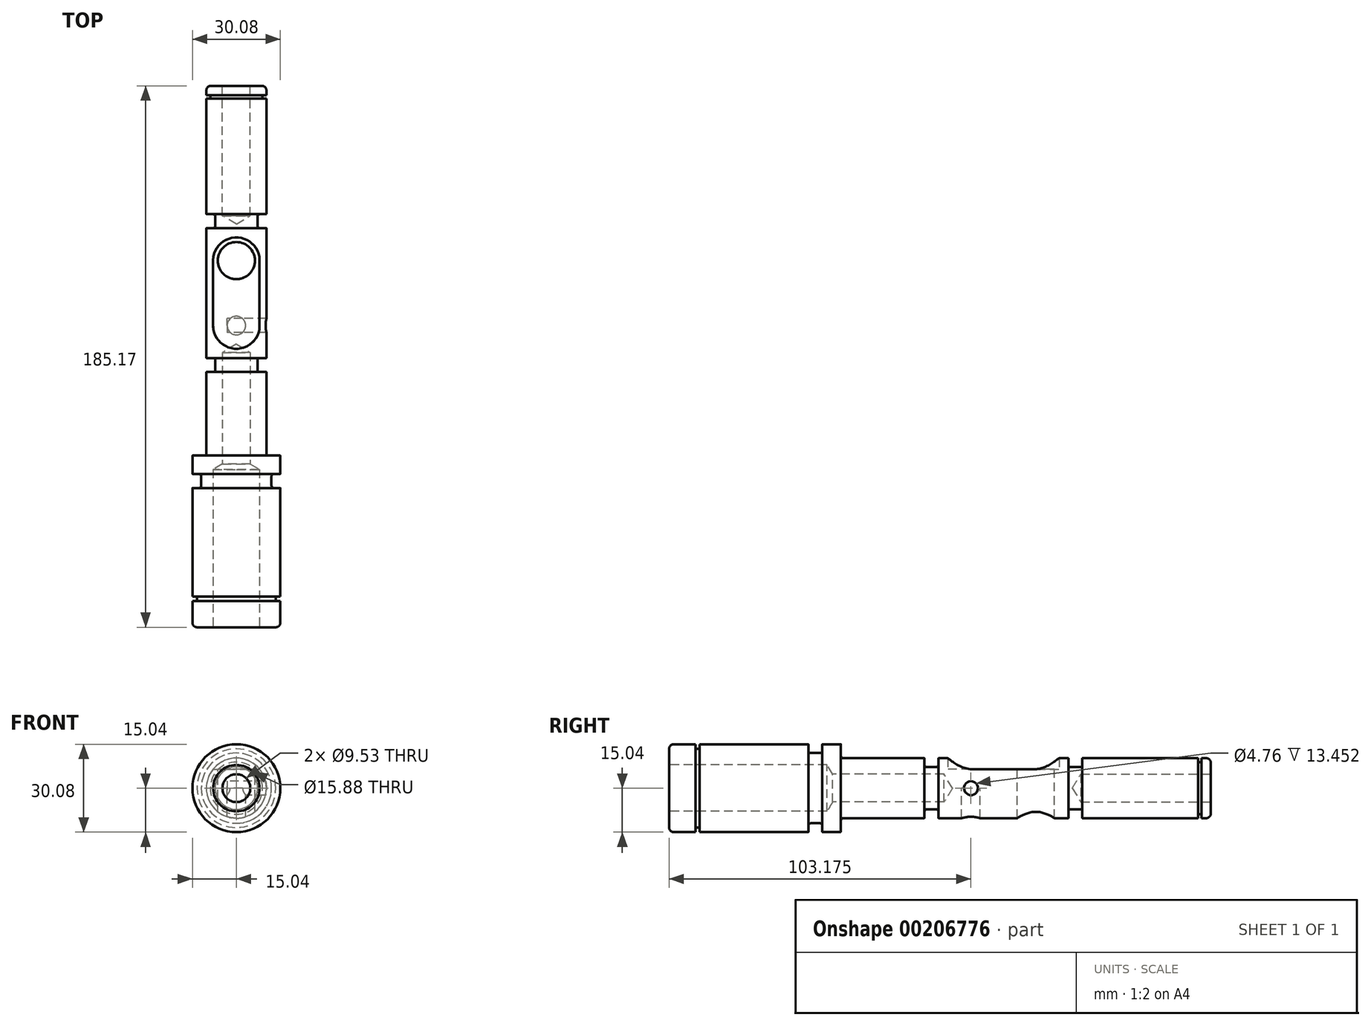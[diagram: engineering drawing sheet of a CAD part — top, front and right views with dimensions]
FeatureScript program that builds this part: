
annotation { "Feature Type Name" : "Feature", "Feature Type Description" : "" }
export const myFeature = defineFeature(function(context is Context, id is Id, definition is map)
    precondition{}
    {
        {
            var Q0;
            Q0=qCreatedBy(makeId("Right.planeOp"),FACE);
            var sketch = newSketch(context, id + "F0", { "sketchPlane" : qUnion([Q0])});
            skLineSegment(sketch, "E0", {"start": v(0, 0) * mm, "end": v(0, 15.04) * mm});
            skLineSegment(sketch, "E1", {"start": v(0, 15.04) * mm, "end": v(9.02, 15.04) * mm});
            skLineSegment(sketch, "E2", {"start": v(47.63, 12) * mm, "end": v(47.63, 15.04) * mm});
            skLineSegment(sketch, "E3", {"start": v(47.63, 12) * mm, "end": v(52.37, 12) * mm});
            skLineSegment(sketch, "E4", {"start": v(52.37, 15.04) * mm, "end": v(52.37, 12) * mm});
            skLineSegment(sketch, "E5", {"start": v(52.37, 15.04) * mm, "end": v(58.72, 15.04) * mm});
            skLineSegment(sketch, "E6", {"start": v(87.3, 10.27) * mm, "end": v(87.3, 7.24) * mm});
            skLineSegment(sketch, "E7", {"start": v(87.3, 7.24) * mm, "end": v(92.05, 7.24) * mm});
            skLineSegment(sketch, "E8", {"start": v(92.05, 7.24) * mm, "end": v(92.05, 10.27) * mm});
            skLineSegment(sketch, "E9", {"start": v(58.72, 15.04) * mm, "end": v(58.72, 10.27) * mm});
            skLineSegment(sketch, "E10", {"start": v(58.72, 10.27) * mm, "end": v(87.3, 10.27) * mm});
            skLineSegment(sketch, "E11", {"start": v(92.05, 10.27) * mm, "end": v(136.5, 10.27) * mm});
            skLineSegment(sketch, "E12", {"start": v(136.5, 10.27) * mm, "end": v(136.5, 7.24) * mm});
            skLineSegment(sketch, "E13", {"start": v(136.5, 7.24) * mm, "end": v(141.25, 7.24) * mm});
            skLineSegment(sketch, "E14", {"start": v(141.25, 7.24) * mm, "end": v(141.25, 10.27) * mm});
            skLineSegment(sketch, "E15", {"start": v(185.17, 10.27) * mm, "end": v(185.17, 0) * mm});
            skLineSegment(sketch, "E16", {"start": v(0, 0) * mm, "end": v(185.17, 0) * mm});
            skLineSegment(sketch, "E17", {"start": v(10.44, 15.04) * mm, "end": v(10.44, 13.45) * mm});
            skLineSegment(sketch, "E18", {"start": v(10.44, 13.45) * mm, "end": v(9.02, 13.45) * mm});
            skLineSegment(sketch, "E19", {"start": v(9.02, 13.45) * mm, "end": v(9.02, 15.04) * mm});
            skLineSegment(sketch, "E20.trimOffspring", {"start": v(10.44, 15.04) * mm, "end": v(47.63, 15.04) * mm});
            skLineSegment(sketch, "E21", {"start": v(185.17, 10.27) * mm, "end": v(182, 10.27) * mm});
            skLineSegment(sketch, "E22", {"start": v(180.82, 10.27) * mm, "end": v(180.82, 8.94) * mm});
            skLineSegment(sketch, "E23", {"start": v(180.82, 8.94) * mm, "end": v(182, 8.94) * mm});
            skLineSegment(sketch, "E24", {"start": v(182, 8.94) * mm, "end": v(182, 10.27) * mm});
            skLineSegment(sketch, "E25.trimOffspring", {"start": v(180.82, 10.27) * mm, "end": v(141.25, 10.27) * mm});
            skSolve(sketch);
        }
        {
            var Q0;
            Q0=makeQuery(id+"F0.imprint","IMPRINT",FACE,{"disambiguationData":[TD([[makeQuery(id+"F0.imprint","IMPRINT",EDGE,{"derivedFrom":sQuery(id+"F0.wireOp",EDGE,"E0")}),-1.0]])]});
            var Q1;
            Q1=sQuery(id+"F0.wireOp",EDGE,"E0");
            var Q2;
            Q2=sQuery(id+"F0.wireOp",EDGE,"E1");
            var Q3;
            Q3=sQuery(id+"F0.wireOp",EDGE,"E2");
            var Q4;
            Q4=sQuery(id+"F0.wireOp",EDGE,"E3");
            var Q5;
            Q5=sQuery(id+"F0.wireOp",EDGE,"E4");
            var Q6;
            Q6=sQuery(id+"F0.wireOp",EDGE,"E5");
            var Q7;
            Q7=sQuery(id+"F0.wireOp",EDGE,"E9");
            var Q8;
            Q8=sQuery(id+"F0.wireOp",EDGE,"E10");
            var Q9;
            Q9=sQuery(id+"F0.wireOp",EDGE,"E6");
            var Q10;
            Q10=sQuery(id+"F0.wireOp",EDGE,"E7");
            var Q11;
            Q11=sQuery(id+"F0.wireOp",EDGE,"E8");
            var Q12;
            Q12=sQuery(id+"F0.wireOp",EDGE,"E11");
            var Q13;
            Q13=sQuery(id+"F0.wireOp",EDGE,"E14");
            var Q14;
            Q14=sQuery(id+"F0.wireOp",EDGE,"E13");
            var Q15;
            Q15=sQuery(id+"F0.wireOp",EDGE,"E12");
            var Q16;
            Q16=sQuery(id+"F0.wireOp",EDGE,"e7rDd8XX-V8fj-rX7r-6Z2d-5Uji8izavtl3");
            var Q17;
            Q17=sQuery(id+"F0.wireOp",EDGE,"E15");
            var Q18;
            Q18=sQuery(id+"F0.wireOp",EDGE,"E16");
            revolve(context, id + "F1", {"entities" : qUnion([Q0]), "surfaceEntities" : qUnion([Q1, Q2, Q3, Q4, Q5, Q6, Q7, Q8, Q9, Q10, Q11, Q12, Q13, Q14, Q15, Q16, Q17]), "axis" : qUnion([Q18]), "revolveType" : RevolveType.FULL});
        }
        {
            var Q0;
            Q0=qCreatedBy(makeId("Top.planeOp"),FACE);
            var sketch = newSketch(context, id + "F2", { "sketchPlane" : qUnion([Q0])});
            skLineSegment(sketch, "E26", {"start": v(10.27, 92.05) * mm, "end": v(10.27, 136.5) * mm, "construction": true});
            skLineSegment(sketch, "E27", {"start": v(10.27, 92.05) * mm, "end": v(-10.27, 136.5) * mm, "construction": true});
            skLineSegment(sketch, "E28", {"start": v(0, 114.27) * mm, "end": v(0, 92.05) * mm, "construction": true});
            skCircle(sketch, "E29", {"center": v(0, 103.17) * mm, "radius": 6.35 * mm, "construction": true});
            skLineSegment(sketch, "E30", {"start": v(0, 114.27) * mm, "end": v(10.27, 114.27) * mm, "construction": true});
            skCircle(sketch, "E31.MirrorC", {"center": v(0, 125.37) * mm, "radius": 6.35 * mm});
            skSolve(sketch);
        }
        {
            var Q0;
            Q0 = qSketchRegion(id + "F2", true);
            extrude(context, id + "F3", {"entities" : qUnion([Q0]), "operationType" : NewBodyOperationType.REMOVE, "endBound" : BoundingType.THROUGH_ALL, "oppositeDirection" : true, "depth" : 25.4 * mm, "hasSecondDirection" : true, "secondDirectionBound" : SecondDirectionBoundingType.THROUGH_ALL, "secondDirectionOppositeDirection" : false, "secondDirectionDepth" : 25.4 * mm});
        }
        {
            var Q0;
            Q0=makeQuery(id+"F1.opRevolve","SWEPT_FACE",FACE,{"disambiguationData":[OSD([sQuery(id+"F0.wireOp",EDGE,"E0")])]});
            var sketch = newSketch(context, id + "F4", { "sketchPlane" : qUnion([Q0])});
            skPoint(sketch, "E32", {"position": v(0, 0) * mm});
            skSolve(sketch);
        }
        {
            var Q0;
            Q0=sQuery(id+"F4.wireOp",VERTEX,"E32");
            var Q1;
            Q1=makeQuery(id+"F1.opRevolve","SWEPT_BODY",BODY,{"disambiguationData":[OSD([sQuery(id+"F0.wireOp",EDGE,"E0"),sQuery(id+"F0.wireOp",EDGE,"E1"),sQuery(id+"F0.wireOp",EDGE,"E2"),sQuery(id+"F0.wireOp",EDGE,"E3"),sQuery(id+"F0.wireOp",EDGE,"E4"),sQuery(id+"F0.wireOp",EDGE,"E5"),sQuery(id+"F0.wireOp",EDGE,"E6"),sQuery(id+"F0.wireOp",EDGE,"E7"),sQuery(id+"F0.wireOp",EDGE,"E8"),sQuery(id+"F0.wireOp",EDGE,"E9"),sQuery(id+"F0.wireOp",EDGE,"E10"),sQuery(id+"F0.wireOp",EDGE,"E11"),sQuery(id+"F0.wireOp",EDGE,"E12"),sQuery(id+"F0.wireOp",EDGE,"E13"),sQuery(id+"F0.wireOp",EDGE,"E14"),sQuery(id+"F0.wireOp",EDGE,"E15"),sQuery(id+"F0.wireOp",EDGE,"E16"),sQuery(id+"F0.wireOp",EDGE,"E17"),sQuery(id+"F0.wireOp",EDGE,"E18"),sQuery(id+"F0.wireOp",EDGE,"E19"),sQuery(id+"F0.wireOp",EDGE,"E20.trimOffspring"),sQuery(id+"F0.wireOp",EDGE,"E21"),sQuery(id+"F0.wireOp",EDGE,"E22"),sQuery(id+"F0.wireOp",EDGE,"E23"),sQuery(id+"F0.wireOp",EDGE,"E24"),sQuery(id+"F0.wireOp",EDGE,"E25.trimOffspring")])]});
            hole(context, id + "F5", {"style" : HoleStyle.SIMPLE, "endStyle" : HoleEndStyle.BLIND, "holeDiameter" : 15.88 * mm, "holeDepth" : 53.97 * mm, "locations" : qUnion([Q0]), "scope" : qUnion([Q1])});
        }
        {
            var Q0;
            Q0=makeQuery(id+"F1.opRevolve","SWEPT_FACE",FACE,{"disambiguationData":[OSD([sQuery(id+"F0.wireOp",EDGE,"E15")])]});
            var sketch = newSketch(context, id + "F6", { "sketchPlane" : qUnion([Q0])});
            skPoint(sketch, "E33", {"position": v(0, 0) * mm});
            skSolve(sketch);
        }
        {
            var Q0;
            Q0=sQuery(id+"F6.wireOp",VERTEX,"E33");
            var Q1;
            Q1=makeQuery(id+"F1.opRevolve","SWEPT_BODY",BODY,{"disambiguationData":[OSD([sQuery(id+"F0.wireOp",EDGE,"E0"),sQuery(id+"F0.wireOp",EDGE,"E1"),sQuery(id+"F0.wireOp",EDGE,"E2"),sQuery(id+"F0.wireOp",EDGE,"E3"),sQuery(id+"F0.wireOp",EDGE,"E4"),sQuery(id+"F0.wireOp",EDGE,"E5"),sQuery(id+"F0.wireOp",EDGE,"E6"),sQuery(id+"F0.wireOp",EDGE,"E7"),sQuery(id+"F0.wireOp",EDGE,"E8"),sQuery(id+"F0.wireOp",EDGE,"E9"),sQuery(id+"F0.wireOp",EDGE,"E10"),sQuery(id+"F0.wireOp",EDGE,"E11"),sQuery(id+"F0.wireOp",EDGE,"E12"),sQuery(id+"F0.wireOp",EDGE,"E13"),sQuery(id+"F0.wireOp",EDGE,"E14"),sQuery(id+"F0.wireOp",EDGE,"E15"),sQuery(id+"F0.wireOp",EDGE,"E16"),sQuery(id+"F0.wireOp",EDGE,"E17"),sQuery(id+"F0.wireOp",EDGE,"E18"),sQuery(id+"F0.wireOp",EDGE,"E19"),sQuery(id+"F0.wireOp",EDGE,"E20.trimOffspring"),sQuery(id+"F0.wireOp",EDGE,"E21"),sQuery(id+"F0.wireOp",EDGE,"E22"),sQuery(id+"F0.wireOp",EDGE,"E23"),sQuery(id+"F0.wireOp",EDGE,"E24"),sQuery(id+"F0.wireOp",EDGE,"E25.trimOffspring")])]});
            hole(context, id + "F7", {"style" : HoleStyle.SIMPLE, "endStyle" : HoleEndStyle.BLIND, "holeDiameter" : 9.52 * mm, "holeDepth" : 44.45 * mm, "locations" : qUnion([Q0]), "scope" : qUnion([Q1])});
        }
        {
            var Q0;
            Q0=sQuery(id+"F4.wireOp",VERTEX,"E32");
            var Q1;
            Q1=makeQuery(id+"F1.opRevolve","SWEPT_BODY",BODY,{"disambiguationData":[OSD([sQuery(id+"F0.wireOp",EDGE,"E0"),sQuery(id+"F0.wireOp",EDGE,"E1"),sQuery(id+"F0.wireOp",EDGE,"E2"),sQuery(id+"F0.wireOp",EDGE,"E3"),sQuery(id+"F0.wireOp",EDGE,"E4"),sQuery(id+"F0.wireOp",EDGE,"E5"),sQuery(id+"F0.wireOp",EDGE,"E6"),sQuery(id+"F0.wireOp",EDGE,"E7"),sQuery(id+"F0.wireOp",EDGE,"E8"),sQuery(id+"F0.wireOp",EDGE,"E9"),sQuery(id+"F0.wireOp",EDGE,"E10"),sQuery(id+"F0.wireOp",EDGE,"E11"),sQuery(id+"F0.wireOp",EDGE,"E12"),sQuery(id+"F0.wireOp",EDGE,"E13"),sQuery(id+"F0.wireOp",EDGE,"E14"),sQuery(id+"F0.wireOp",EDGE,"E15"),sQuery(id+"F0.wireOp",EDGE,"E16"),sQuery(id+"F0.wireOp",EDGE,"E17"),sQuery(id+"F0.wireOp",EDGE,"E18"),sQuery(id+"F0.wireOp",EDGE,"E19"),sQuery(id+"F0.wireOp",EDGE,"E20.trimOffspring"),sQuery(id+"F0.wireOp",EDGE,"E21"),sQuery(id+"F0.wireOp",EDGE,"E22"),sQuery(id+"F0.wireOp",EDGE,"E23"),sQuery(id+"F0.wireOp",EDGE,"E24"),sQuery(id+"F0.wireOp",EDGE,"E25.trimOffspring")])]});
            hole(context, id + "F8", {"style" : HoleStyle.SIMPLE, "endStyle" : HoleEndStyle.BLIND, "holeDiameter" : 9.52 * mm, "holeDepth" : 38.1 * mm, "locations" : qUnion([Q0]), "scope" : qUnion([Q1])});
        }
        {
            var Q0;
            Q0=qCreatedBy(makeId("Top.planeOp"),FACE);
            var sketch = newSketch(context, id + "F9", { "sketchPlane" : qUnion([Q0])});
            skLineSegment(sketch, "E34", {"start": v(0, 125.37) * mm, "end": v(0, 103.17) * mm});
            skArc(sketch, "E35.0.startCap", {"start": v(-7.94, 125.37) * mm, "mid": v(0, 133.31) * mm, "end": v(7.94, 125.37) * mm});
            skArc(sketch, "E35.0.endCap", {"start": v(7.94, 103.17) * mm, "mid": v(0, 95.24) * mm, "end": v(-7.94, 103.17) * mm});
            skLineSegment(sketch, "E35.0.left", {"start": v(7.94, 125.37) * mm, "end": v(7.94, 103.17) * mm});
            skLineSegment(sketch, "E35.0.right", {"start": v(-7.94, 125.37) * mm, "end": v(-7.94, 103.17) * mm});
            skSolve(sketch);
        }
        {
            var Q0;
            Q0 = qSketchRegion(id + "F9", true);
            var Q1;
            Q1=makeQuery(id+"F1.opRevolve","SWEPT_FACE",FACE,{"disambiguationData":[OSD([sQuery(id+"F0.wireOp",EDGE,"E11")])]});
            extrude(context, id + "F10", {"entities" : qUnion([Q0]), "operationType" : NewBodyOperationType.REMOVE, "endBound" : BoundingType.UP_TO_SURFACE, "endBoundEntityFace" : qUnion([Q1]), "depth" : 25.4 * mm, "hasSecondDirection" : true, "secondDirectionOppositeDirection" : false, "secondDirectionDepth" : 6.53 * mm});
        }
        {
            var Q0;
            Q0=qCreatedBy(makeId("Right.planeOp"),FACE);
            var sketch = newSketch(context, id + "F11", { "sketchPlane" : qUnion([Q0])});
            skCircle(sketch, "E36", {"center": v(103.17, 0) * mm, "radius": 2.38 * mm});
            skSolve(sketch);
        }
        {
            var Q0;
            Q0 = qSketchRegion(id + "F11", true);
            var Q1;
            Q1=makeQuery(id+"F1.opRevolve","SWEPT_FACE",FACE,{"disambiguationData":[OSD([sQuery(id+"F0.wireOp",EDGE,"E11")])]});
            extrude(context, id + "F12", {"entities" : qUnion([Q0]), "operationType" : NewBodyOperationType.REMOVE, "endBound" : BoundingType.UP_TO_SURFACE, "endBoundEntityFace" : qUnion([Q1]), "depth" : 25.4 * mm, "hasSecondDirection" : true, "secondDirectionOppositeDirection" : true, "secondDirectionDepth" : 3.17 * mm});
        }
        {
            var Q0;
            Q0=qCreatedBy(makeId("Top.planeOp"),FACE);
            var sketch = newSketch(context, id + "F13", { "sketchPlane" : qUnion([Q0])});
            skCircle(sketch, "E37", {"center": v(0, 103.17) * mm, "radius": 3.18 * mm});
            skSolve(sketch);
        }
        {
            var Q0;
            Q0 = qSketchRegion(id + "F13", true);
            var Q1;
            Q1=makeQuery(id+"F1.opRevolve","SWEPT_FACE",FACE,{"disambiguationData":[OSD([sQuery(id+"F0.wireOp",EDGE,"E11")])]});
            extrude(context, id + "F14", {"entities" : qUnion([Q0]), "operationType" : NewBodyOperationType.REMOVE, "endBound" : BoundingType.UP_TO_SURFACE, "oppositeDirection" : true, "endBoundEntityFace" : qUnion([Q1]), "depth" : 25.4 * mm});
        }
        {
            var Q0;
            Q0=makeQuery(id+"F1.opRevolve","SWEPT_EDGE",EDGE,{"disambiguationData":[OSD([sQuery(id+"F0.wireOp",EDGE,"E6"),sQuery(id+"F0.wireOp",EDGE,"E10")])]});
            var Q1;
            Q1=makeQuery(id+"F1.opRevolve","SWEPT_EDGE",EDGE,{"disambiguationData":[OSD([sQuery(id+"F0.wireOp",EDGE,"E8"),sQuery(id+"F0.wireOp",EDGE,"E11")])]});
            var Q2;
            Q2=makeQuery(id+"F1.opRevolve","SWEPT_EDGE",EDGE,{"disambiguationData":[OSD([sQuery(id+"F0.wireOp",EDGE,"E11"),sQuery(id+"F0.wireOp",EDGE,"E12")])]});
            var Q3;
            Q3=makeQuery(id+"F1.opRevolve","SWEPT_EDGE",EDGE,{"disambiguationData":[OSD([sQuery(id+"F0.wireOp",EDGE,"E14"),sQuery(id+"F0.wireOp",EDGE,"E25.trimOffspring")])]});
            var Q4;
            Q4=makeQuery(id+"F1.opRevolve","SWEPT_EDGE",EDGE,{"disambiguationData":[OSD([sQuery(id+"F0.wireOp",EDGE,"E2"),sQuery(id+"F0.wireOp",EDGE,"E20.trimOffspring")])]});
            var Q5;
            Q5=makeQuery(id+"F1.opRevolve","SWEPT_EDGE",EDGE,{"disambiguationData":[OSD([sQuery(id+"F0.wireOp",EDGE,"E4"),sQuery(id+"F0.wireOp",EDGE,"E5")])]});
            var Q6;
            Q6=makeQuery(id+"F1.opRevolve","SWEPT_EDGE",EDGE,{"disambiguationData":[OSD([sQuery(id+"F0.wireOp",EDGE,"E5"),sQuery(id+"F0.wireOp",EDGE,"E9")])]});
            fillet(context, id + "F15", {"entities" : qUnion([Q0, Q1, Q2, Q3, Q4, Q5, Q6]), "radius" : 0.13 * mm, "tangentPropagation" : true, "allowEdgeOverflow" : false});
        }
        {
            var Q0;
            Q0=makeQuery(id+"F1.opRevolve","SWEPT_EDGE",EDGE,{"disambiguationData":[OSD([sQuery(id+"F0.wireOp",EDGE,"E6"),sQuery(id+"F0.wireOp",EDGE,"E7")])]});
            var Q1;
            Q1=makeQuery(id+"F1.opRevolve","SWEPT_EDGE",EDGE,{"disambiguationData":[OSD([sQuery(id+"F0.wireOp",EDGE,"E7"),sQuery(id+"F0.wireOp",EDGE,"E8")])]});
            var Q2;
            Q2=makeQuery(id+"F1.opRevolve","SWEPT_EDGE",EDGE,{"disambiguationData":[OSD([sQuery(id+"F0.wireOp",EDGE,"E13"),sQuery(id+"F0.wireOp",EDGE,"E14")])]});
            var Q3;
            Q3=makeQuery(id+"F1.opRevolve","SWEPT_EDGE",EDGE,{"disambiguationData":[OSD([sQuery(id+"F0.wireOp",EDGE,"E12"),sQuery(id+"F0.wireOp",EDGE,"E13")])]});
            var Q4;
            Q4=makeQuery(id+"F1.opRevolve","SWEPT_EDGE",EDGE,{"disambiguationData":[OSD([sQuery(id+"F0.wireOp",EDGE,"E2"),sQuery(id+"F0.wireOp",EDGE,"E3")])]});
            var Q5;
            Q5=makeQuery(id+"F1.opRevolve","SWEPT_EDGE",EDGE,{"disambiguationData":[OSD([sQuery(id+"F0.wireOp",EDGE,"E3"),sQuery(id+"F0.wireOp",EDGE,"E4")])]});
            var Q6;
            Q6=makeQuery(id+"F1.opRevolve","SWEPT_EDGE",EDGE,{"disambiguationData":[OSD([sQuery(id+"F0.wireOp",EDGE,"E9"),sQuery(id+"F0.wireOp",EDGE,"E10")])]});
            fillet(context, id + "F16", {"entities" : qUnion([Q0, Q1, Q2, Q3, Q4, Q5, Q6]), "radius" : 0.76 * mm, "tangentPropagation" : true, "allowEdgeOverflow" : false});
        }
        {
            var Q0;
            Q0=makeQuery(id+"F1.opRevolve","SWEPT_EDGE",EDGE,{"disambiguationData":[OSD([sQuery(id+"F0.wireOp",EDGE,"E0"),sQuery(id+"F0.wireOp",EDGE,"E1")])]});
            var Q1;
            Q1=makeQuery(id+"F1.opRevolve","SWEPT_EDGE",EDGE,{"disambiguationData":[OSD([sQuery(id+"F0.wireOp",EDGE,"E15"),sQuery(id+"F0.wireOp",EDGE,"E21")])]});
            fillet(context, id + "F17", {"entities" : qUnion([Q0, Q1]), "radius" : 1.59 * mm, "tangentPropagation" : true, "allowEdgeOverflow" : false});
        }
    });
